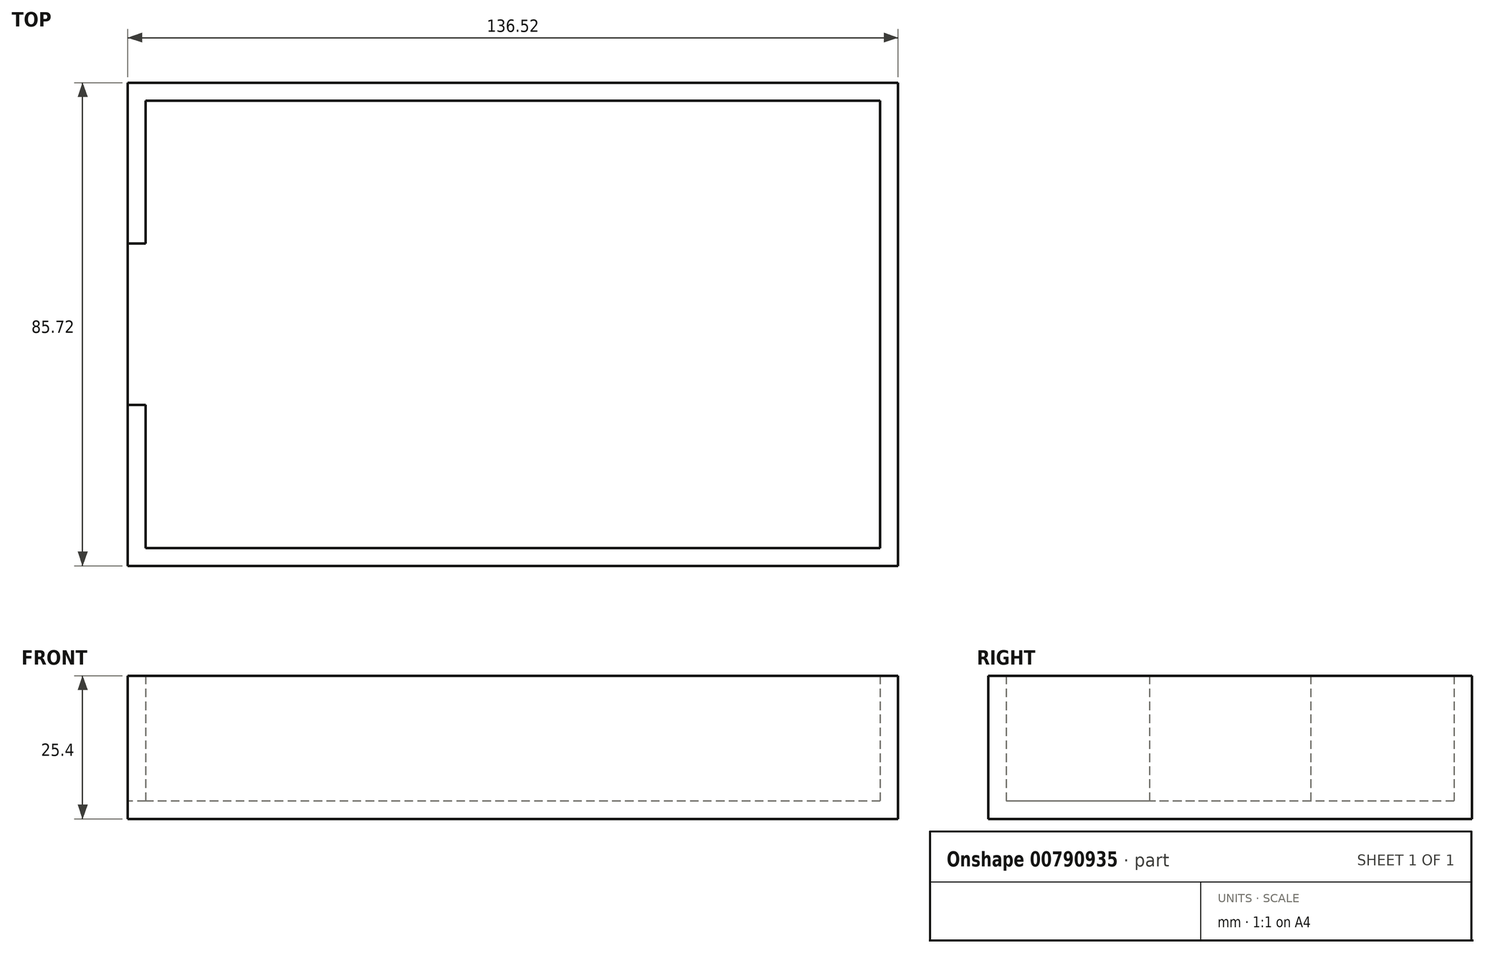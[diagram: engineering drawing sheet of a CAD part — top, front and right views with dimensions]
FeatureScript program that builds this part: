
annotation { "Feature Type Name" : "Feature", "Feature Type Description" : "" }
export const myFeature = defineFeature(function(context is Context, id is Id, definition is map)
    precondition{}
    {
        {
            var Q0;
            Q0=qCreatedBy(makeId("Top.planeOp"),FACE);
            var sketch = newSketch(context, id + "F0", { "sketchPlane" : qUnion([Q0])});
            skLineSegment(sketch, "E0.bottom", {"start": v(62.2, 39.69) * mm, "end": v(-67.98, 39.69) * mm});
            skLineSegment(sketch, "E0.top", {"start": v(62.2, -39.69) * mm, "end": v(-67.98, -39.69) * mm});
            skLineSegment(sketch, "E0.left", {"start": v(62.2, 39.69) * mm, "end": v(62.2, -39.69) * mm});
            skLineSegment(sketch, "E0.right", {"start": v(-67.98, 39.69) * mm, "end": v(-67.98, -39.69) * mm});
            skPoint(sketch, "E0.middle", {"position": v(-2.9, 0) * mm});
            skLineSegment(sketch, "E1.0", {"start": v(65.37, 42.86) * mm, "end": v(-71.15, 42.86) * mm});
            skLineSegment(sketch, "E1.1", {"start": v(65.37, 42.86) * mm, "end": v(65.37, -42.86) * mm});
            skLineSegment(sketch, "E1.2", {"start": v(65.37, -42.86) * mm, "end": v(-71.15, -42.86) * mm});
            skLineSegment(sketch, "E1.3", {"start": v(-71.15, 42.86) * mm, "end": v(-71.15, -42.86) * mm});
            skLineSegment(sketch, "E2", {"start": v(-67.98, -39.69) * mm, "end": v(-2.9, -39.69) * mm});
            skLineSegment(sketch, "E3", {"start": v(-67.98, 39.69) * mm, "end": v(-67.98, 0) * mm});
            skLineSegment(sketch, "E4.bottom", {"start": v(-67.98, -39.69) * mm, "end": v(-67.98, -39.69) * mm});
            skLineSegment(sketch, "E4.top", {"start": v(-67.98, 0) * mm, "end": v(-67.98, 0) * mm});
            skLineSegment(sketch, "E4.left", {"start": v(-67.98, -39.69) * mm, "end": v(-67.98, 0) * mm});
            skLineSegment(sketch, "E4.right", {"start": v(-67.98, -39.69) * mm, "end": v(-67.98, 0) * mm});
            skLineSegment(sketch, "E5", {"start": v(-67.98, 0) * mm, "end": v(-67.98, -14.3) * mm});
            skLineSegment(sketch, "E6", {"start": v(-67.98, 0) * mm, "end": v(-67.98, 14.3) * mm});
            skLineSegment(sketch, "E7", {"start": v(-67.98, 14.3) * mm, "end": v(-71.15, 14.3) * mm});
            skLineSegment(sketch, "E8", {"start": v(-67.98, -14.3) * mm, "end": v(-71.15, -14.3) * mm});
            skSolve(sketch);
        }
        {
            var Q0;
            {var subQ5=sQuery(id+"F0.wireOp",EDGE,"E0.bottom");Q0=makeQuery(id+"F0.imprint","IMPRINT",FACE,{"disambiguationData":[TD([[makeQuery(id+"F0.imprint","IMPRINT",EDGE,{"derivedFrom":subQ5}),1.0]])]});}
            var Q1;
            {var subQ0=sQuery(id+"F0.wireOp",EDGE,"E7");Q1=makeQuery(id+"F0.imprint","IMPRINT",FACE,{"disambiguationData":[TD([[makeQuery(id+"F0.imprint","IMPRINT",EDGE,{"derivedFrom":subQ0}),1.0]])]});}
            extrude(context, id + "F1", {"entities" : qUnion([Q0, Q1]), "depth" : 3.17 * mm, "offsetDistance" : 25.4 * mm});
        }
        {
            var Q0;
            {var subQ3=sQuery(id+"F0.wireOp",EDGE,"E0.bottom");Q0=makeQuery(id+"F0.imprint","IMPRINT",FACE,{"disambiguationData":[TD([[makeQuery(id+"F0.imprint","IMPRINT",EDGE,{"derivedFrom":subQ3}),-1.0]])]});}
            extrude(context, id + "F2", {"entities" : qUnion([Q0]), "operationType" : NewBodyOperationType.ADD, "depth" : 25.4 * mm, "offsetDistance" : 25.4 * mm});
        }
    });
